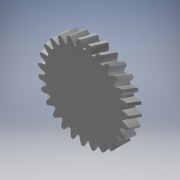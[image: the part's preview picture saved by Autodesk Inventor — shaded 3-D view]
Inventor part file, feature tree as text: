
AUTODESK INVENTOR PART (.ipt)
format: ipt  version: 2019 (Build 230136000, 136)  size: 459,264 bytes
history: native  units: mm (DEFAULTED — no unit token found)
features: plane x3, other x3, sketch x2, extrude x1
ambient origin geometry x8: Origin, YZ Plane, XZ Plane, XY Plane, X Axis, Y Axis, Z Axis, Center Point
bodies: Solid1 (feature_tree)
feature tree (9):
  extrude  "Extrusion1"  Depth=5.0mm TaperAngle=0.0deg
  plane  "Work Plane2"
  plane  "Work Plane8"
  plane  "Work Plane9"
  other  "Spur Gear"
  sketch  "Sketch1"  dims[d0=34.130032mm d1=5.0mm d2=0.0mm]
  sketch  "Sketch2"  dims[d3=31.880377mm d4=10.0mm d5=0.0mm d16=31.29mm d17=0.0mm d34=1.163553mm d39=0.0mm d41=0.0mm d43=31.29mm d46=31.29mm d47=0.0mm d48=0.0mm]
  other  "Srf1"
  other  "Pitch Diameter"
